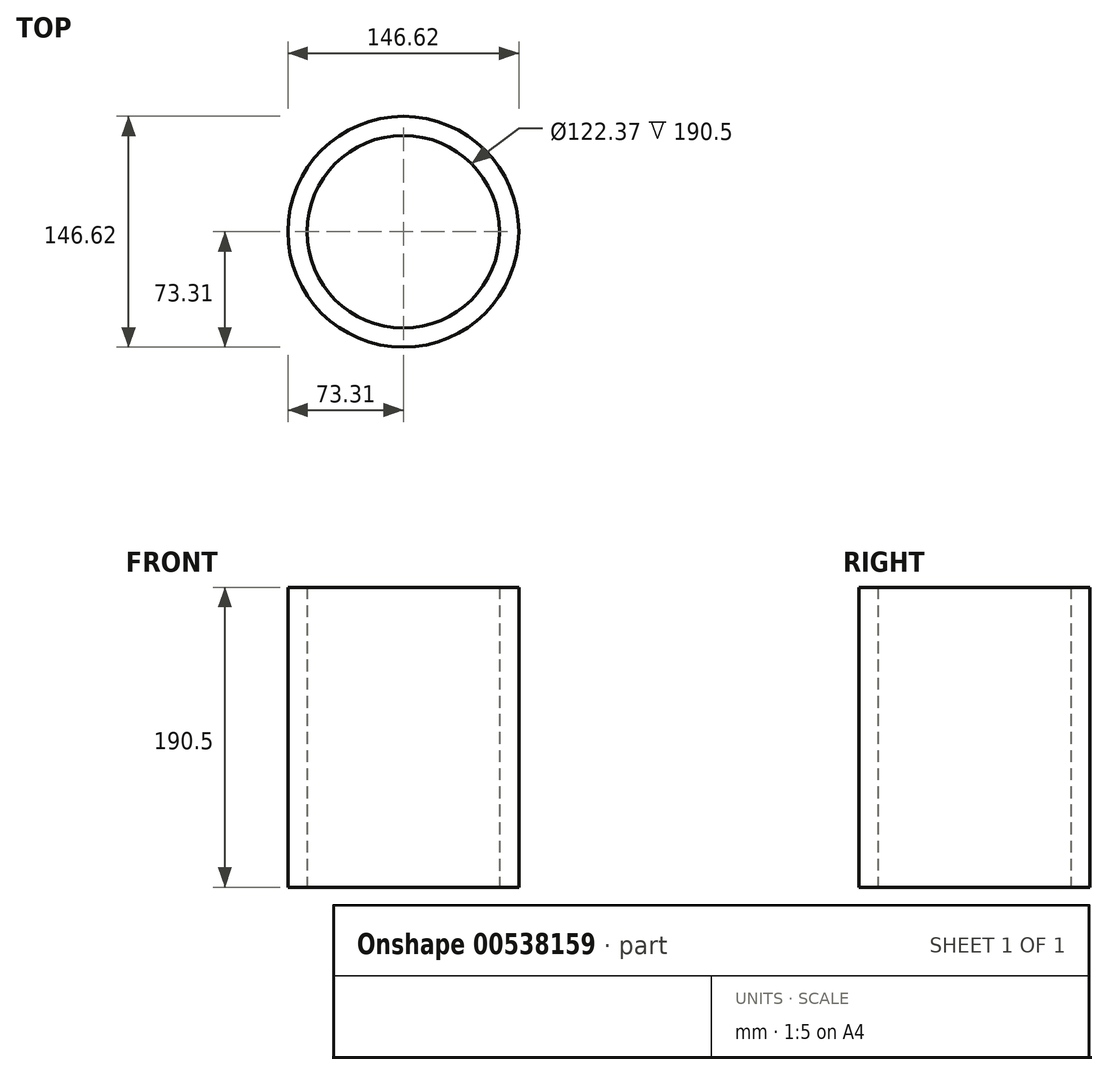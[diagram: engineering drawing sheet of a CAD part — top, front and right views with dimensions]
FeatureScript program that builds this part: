
annotation { "Feature Type Name" : "Feature", "Feature Type Description" : "" }
export const myFeature = defineFeature(function(context is Context, id is Id, definition is map)
    precondition{}
    {
        {
            var Q0;
            Q0=qCreatedBy(makeId("Top.planeOp"),FACE);
            var sketch = newSketch(context, id + "F0", { "sketchPlane" : qUnion([Q0])});
            skCircle(sketch, "E0", {"center": v(0, 0) * mm, "radius": 61.18 * mm});
            skCircle(sketch, "E1", {"center": v(0, 0) * mm, "radius": 73.3 * mm});
            skSolve(sketch);
        }
        {
            var Q0;
            Q0 = qSketchRegion(id + "F0", true);
            extrude(context, id + "F1", {"entities" : qUnion([Q0]), "depth" : 190.5 * mm, "offsetDistance" : 25.4 * mm});
        }
    });
